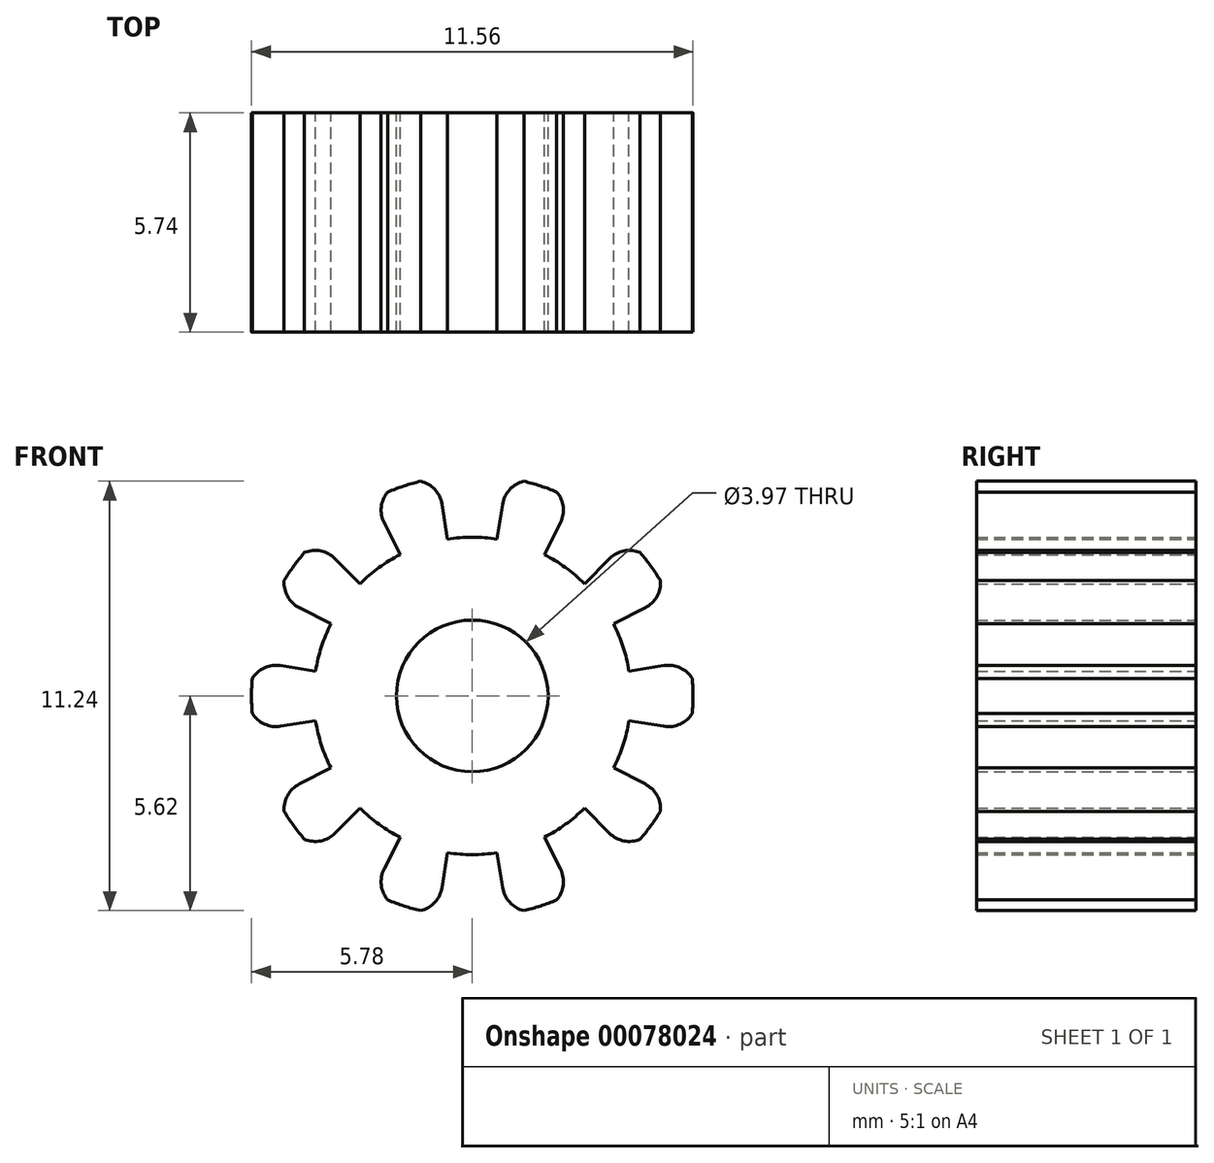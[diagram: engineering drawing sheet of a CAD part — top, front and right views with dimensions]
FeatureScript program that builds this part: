
annotation { "Feature Type Name" : "Feature", "Feature Type Description" : "" }
export const myFeature = defineFeature(function(context is Context, id is Id, definition is map)
    precondition{}
    {
        {
            var Q0;
            Q0=qCreatedBy(makeId("Front.planeOp"),FACE);
            var sketch = newSketch(context, id + "F0", { "sketchPlane" : qUnion([Q0])});
            skCircle(sketch, "E0", {"center": v(0, 0) * mm, "radius": 5.78 * mm, "construction": true});
            skCircle(sketch, "E1", {"center": v(0, 0) * mm, "radius": 5.08 * mm, "construction": true});
            skCircle(sketch, "E2", {"center": v(0, 0) * mm, "radius": 4.15 * mm, "construction": true});
            skLineSegment(sketch, "E3", {"start": v(0, 0) * mm, "end": v(3.95, 1.28) * mm, "construction": true});
            skLineSegment(sketch, "E4", {"start": v(0, 0) * mm, "end": v(6.61, 0) * mm, "construction": true});
            skLineSegment(sketch, "E5", {"start": v(0, 0) * mm, "end": v(6.81, 1.08) * mm, "construction": true});
            skLineSegment(sketch, "E6", {"start": v(0, 0) * mm, "end": v(7.13, 0.56) * mm, "construction": true});
            skArc(sketch, "E7", {"start": v(5.76, 0.45) * mm, "mid": v(5.77, 0.23) * mm, "end": v(5.78, 0) * mm});
            skArc(sketch, "E8", {"start": v(3.95, 1.28) * mm, "mid": v(4.04, 0.97) * mm, "end": v(4.1, 0.65) * mm});
            skLineSegment(sketch, "E9", {"start": v(4.1, 0.65) * mm, "end": v(5.02, 0.8) * mm});
            skArc(sketch, "E10", {"start": v(5.02, 0.8) * mm, "mid": v(5.44, 0.74) * mm, "end": v(5.76, 0.45) * mm});
            skLineSegment(sketch, "E11", {"start": v(0, 0) * mm, "end": v(3.95, 1.28) * mm});
            skLineSegment(sketch, "E12", {"start": v(0, 0) * mm, "end": v(5.78, 0) * mm});
            skArc(sketch, "E13.MirrorCS", {"start": v(3.95, -1.28) * mm, "mid": v(4.04, -0.97) * mm, "end": v(4.1, -0.65) * mm});
            skLineSegment(sketch, "E14.MirrorCS", {"start": v(4.1, -0.65) * mm, "end": v(5.02, -0.8) * mm});
            skArc(sketch, "E15.MirrorCS", {"start": v(5.02, -0.8) * mm, "mid": v(5.44, -0.74) * mm, "end": v(5.76, -0.45) * mm});
            skArc(sketch, "E16.MirrorCS", {"start": v(5.76, -0.45) * mm, "mid": v(5.77, -0.23) * mm, "end": v(5.78, 0) * mm});
            skArc(sketch, "E17.1.0", {"start": v(2.44, 3.36) * mm, "mid": v(2.7, 3.16) * mm, "end": v(2.94, 2.94) * mm});
            skLineSegment(sketch, "E17.1.1", {"start": v(2.94, 2.94) * mm, "end": v(3.6, 3.6) * mm});
            skArc(sketch, "E17.1.2", {"start": v(3.6, 3.6) * mm, "mid": v(3.97, 3.8) * mm, "end": v(4.4, 3.75) * mm});
            skArc(sketch, "E17.1.3", {"start": v(4.4, 3.75) * mm, "mid": v(4.54, 3.58) * mm, "end": v(4.67, 3.4) * mm});
            skArc(sketch, "E17.1.4", {"start": v(4.93, 3.02) * mm, "mid": v(4.8, 3.21) * mm, "end": v(4.67, 3.4) * mm});
            skArc(sketch, "E17.1.5", {"start": v(4.53, 2.3) * mm, "mid": v(4.83, 2.6) * mm, "end": v(4.93, 3.02) * mm});
            skLineSegment(sketch, "E17.1.6", {"start": v(3.7, 1.89) * mm, "end": v(4.53, 2.3) * mm});
            skArc(sketch, "E17.1.7", {"start": v(3.95, 1.28) * mm, "mid": v(3.84, 1.59) * mm, "end": v(3.7, 1.89) * mm});
            skArc(sketch, "E17.2.0", {"start": v(0, 4.15) * mm, "mid": v(0.33, 4.14) * mm, "end": v(0.65, 4.1) * mm});
            skLineSegment(sketch, "E17.2.1", {"start": v(0.65, 4.1) * mm, "end": v(0.8, 5.02) * mm});
            skArc(sketch, "E17.2.2", {"start": v(0.8, 5.02) * mm, "mid": v(0.98, 5.4) * mm, "end": v(1.35, 5.62) * mm});
            skArc(sketch, "E17.2.3", {"start": v(1.35, 5.62) * mm, "mid": v(1.57, 5.56) * mm, "end": v(1.79, 5.5) * mm});
            skArc(sketch, "E17.2.4", {"start": v(2.21, 5.34) * mm, "mid": v(2, 5.42) * mm, "end": v(1.79, 5.5) * mm});
            skArc(sketch, "E17.2.5", {"start": v(2.3, 4.53) * mm, "mid": v(2.38, 4.95) * mm, "end": v(2.21, 5.34) * mm});
            skLineSegment(sketch, "E17.2.6", {"start": v(1.89, 3.7) * mm, "end": v(2.3, 4.53) * mm});
            skArc(sketch, "E17.2.7", {"start": v(2.44, 3.36) * mm, "mid": v(2.17, 3.54) * mm, "end": v(1.89, 3.7) * mm});
            skArc(sketch, "E17.3.0", {"start": v(-2.44, 3.36) * mm, "mid": v(-2.17, 3.54) * mm, "end": v(-1.89, 3.7) * mm});
            skLineSegment(sketch, "E17.3.1", {"start": v(-1.89, 3.7) * mm, "end": v(-2.3, 4.53) * mm});
            skArc(sketch, "E17.3.2", {"start": v(-2.3, 4.53) * mm, "mid": v(-2.38, 4.95) * mm, "end": v(-2.21, 5.34) * mm});
            skArc(sketch, "E17.3.3", {"start": v(-2.21, 5.34) * mm, "mid": v(-2, 5.42) * mm, "end": v(-1.79, 5.5) * mm});
            skArc(sketch, "E17.3.4", {"start": v(-1.35, 5.62) * mm, "mid": v(-1.57, 5.56) * mm, "end": v(-1.79, 5.5) * mm});
            skArc(sketch, "E17.3.5", {"start": v(-0.8, 5.02) * mm, "mid": v(-0.98, 5.4) * mm, "end": v(-1.35, 5.62) * mm});
            skLineSegment(sketch, "E17.3.6", {"start": v(-0.65, 4.1) * mm, "end": v(-0.8, 5.02) * mm});
            skArc(sketch, "E17.3.7", {"start": v(0, 4.15) * mm, "mid": v(-0.33, 4.14) * mm, "end": v(-0.65, 4.1) * mm});
            skArc(sketch, "E17.4.0", {"start": v(-3.95, 1.28) * mm, "mid": v(-3.84, 1.59) * mm, "end": v(-3.7, 1.89) * mm});
            skLineSegment(sketch, "E17.4.1", {"start": v(-3.7, 1.89) * mm, "end": v(-4.53, 2.3) * mm});
            skArc(sketch, "E17.4.2", {"start": v(-4.53, 2.3) * mm, "mid": v(-4.83, 2.6) * mm, "end": v(-4.93, 3.02) * mm});
            skArc(sketch, "E17.4.3", {"start": v(-4.93, 3.02) * mm, "mid": v(-4.8, 3.21) * mm, "end": v(-4.67, 3.4) * mm});
            skArc(sketch, "E17.4.4", {"start": v(-4.4, 3.75) * mm, "mid": v(-4.54, 3.58) * mm, "end": v(-4.67, 3.4) * mm});
            skArc(sketch, "E17.4.5", {"start": v(-3.6, 3.6) * mm, "mid": v(-3.97, 3.8) * mm, "end": v(-4.4, 3.75) * mm});
            skLineSegment(sketch, "E17.4.6", {"start": v(-2.94, 2.94) * mm, "end": v(-3.6, 3.6) * mm});
            skArc(sketch, "E17.4.7", {"start": v(-2.44, 3.36) * mm, "mid": v(-2.7, 3.16) * mm, "end": v(-2.94, 2.94) * mm});
            skArc(sketch, "E17.5.0", {"start": v(-3.95, -1.28) * mm, "mid": v(-4.04, -0.97) * mm, "end": v(-4.1, -0.65) * mm});
            skLineSegment(sketch, "E17.5.1", {"start": v(-4.1, -0.65) * mm, "end": v(-5.02, -0.8) * mm});
            skArc(sketch, "E17.5.2", {"start": v(-5.02, -0.8) * mm, "mid": v(-5.44, -0.74) * mm, "end": v(-5.76, -0.45) * mm});
            skArc(sketch, "E17.5.3", {"start": v(-5.76, -0.45) * mm, "mid": v(-5.77, -0.23) * mm, "end": v(-5.78, 0) * mm});
            skArc(sketch, "E17.5.4", {"start": v(-5.76, 0.45) * mm, "mid": v(-5.77, 0.23) * mm, "end": v(-5.78, 0) * mm});
            skArc(sketch, "E17.5.5", {"start": v(-5.02, 0.8) * mm, "mid": v(-5.44, 0.74) * mm, "end": v(-5.76, 0.45) * mm});
            skLineSegment(sketch, "E17.5.6", {"start": v(-4.1, 0.65) * mm, "end": v(-5.02, 0.8) * mm});
            skArc(sketch, "E17.5.7", {"start": v(-3.95, 1.28) * mm, "mid": v(-4.04, 0.97) * mm, "end": v(-4.1, 0.65) * mm});
            skArc(sketch, "E17.6.0", {"start": v(-2.44, -3.36) * mm, "mid": v(-2.7, -3.16) * mm, "end": v(-2.94, -2.94) * mm});
            skLineSegment(sketch, "E17.6.1", {"start": v(-2.94, -2.94) * mm, "end": v(-3.6, -3.6) * mm});
            skArc(sketch, "E17.6.2", {"start": v(-3.6, -3.6) * mm, "mid": v(-3.97, -3.8) * mm, "end": v(-4.4, -3.75) * mm});
            skArc(sketch, "E17.6.3", {"start": v(-4.4, -3.75) * mm, "mid": v(-4.54, -3.58) * mm, "end": v(-4.67, -3.4) * mm});
            skArc(sketch, "E17.6.4", {"start": v(-4.93, -3.02) * mm, "mid": v(-4.8, -3.21) * mm, "end": v(-4.67, -3.4) * mm});
            skArc(sketch, "E17.6.5", {"start": v(-4.53, -2.3) * mm, "mid": v(-4.83, -2.6) * mm, "end": v(-4.93, -3.02) * mm});
            skLineSegment(sketch, "E17.6.6", {"start": v(-3.7, -1.89) * mm, "end": v(-4.53, -2.3) * mm});
            skArc(sketch, "E17.6.7", {"start": v(-3.95, -1.28) * mm, "mid": v(-3.84, -1.59) * mm, "end": v(-3.7, -1.89) * mm});
            skArc(sketch, "E17.7.0", {"start": v(0, -4.15) * mm, "mid": v(-0.33, -4.14) * mm, "end": v(-0.65, -4.1) * mm});
            skLineSegment(sketch, "E17.7.1", {"start": v(-0.65, -4.1) * mm, "end": v(-0.8, -5.02) * mm});
            skArc(sketch, "E17.7.2", {"start": v(-0.8, -5.02) * mm, "mid": v(-0.98, -5.4) * mm, "end": v(-1.35, -5.62) * mm});
            skArc(sketch, "E17.7.3", {"start": v(-1.35, -5.62) * mm, "mid": v(-1.57, -5.56) * mm, "end": v(-1.79, -5.5) * mm});
            skArc(sketch, "E17.7.4", {"start": v(-2.21, -5.34) * mm, "mid": v(-2, -5.42) * mm, "end": v(-1.79, -5.5) * mm});
            skArc(sketch, "E17.7.5", {"start": v(-2.3, -4.53) * mm, "mid": v(-2.38, -4.95) * mm, "end": v(-2.21, -5.34) * mm});
            skLineSegment(sketch, "E17.7.6", {"start": v(-1.89, -3.7) * mm, "end": v(-2.3, -4.53) * mm});
            skArc(sketch, "E17.7.7", {"start": v(-2.44, -3.36) * mm, "mid": v(-2.17, -3.54) * mm, "end": v(-1.89, -3.7) * mm});
            skArc(sketch, "E17.8.0", {"start": v(2.44, -3.36) * mm, "mid": v(2.17, -3.54) * mm, "end": v(1.89, -3.7) * mm});
            skLineSegment(sketch, "E17.8.1", {"start": v(1.89, -3.7) * mm, "end": v(2.3, -4.53) * mm});
            skArc(sketch, "E17.8.2", {"start": v(2.3, -4.53) * mm, "mid": v(2.38, -4.95) * mm, "end": v(2.21, -5.34) * mm});
            skArc(sketch, "E17.8.3", {"start": v(2.21, -5.34) * mm, "mid": v(2, -5.42) * mm, "end": v(1.79, -5.5) * mm});
            skArc(sketch, "E17.8.4", {"start": v(1.35, -5.62) * mm, "mid": v(1.57, -5.56) * mm, "end": v(1.79, -5.5) * mm});
            skArc(sketch, "E17.8.5", {"start": v(0.8, -5.02) * mm, "mid": v(0.98, -5.4) * mm, "end": v(1.35, -5.62) * mm});
            skLineSegment(sketch, "E17.8.6", {"start": v(0.65, -4.1) * mm, "end": v(0.8, -5.02) * mm});
            skArc(sketch, "E17.8.7", {"start": v(0, -4.15) * mm, "mid": v(0.33, -4.14) * mm, "end": v(0.65, -4.1) * mm});
            skArc(sketch, "E17.9.0", {"start": v(3.95, -1.28) * mm, "mid": v(3.84, -1.59) * mm, "end": v(3.7, -1.89) * mm});
            skLineSegment(sketch, "E17.9.1", {"start": v(3.7, -1.89) * mm, "end": v(4.53, -2.3) * mm});
            skArc(sketch, "E17.9.2", {"start": v(4.53, -2.3) * mm, "mid": v(4.83, -2.6) * mm, "end": v(4.93, -3.02) * mm});
            skArc(sketch, "E17.9.3", {"start": v(4.93, -3.02) * mm, "mid": v(4.8, -3.21) * mm, "end": v(4.67, -3.4) * mm});
            skArc(sketch, "E17.9.4", {"start": v(4.4, -3.75) * mm, "mid": v(4.54, -3.58) * mm, "end": v(4.67, -3.4) * mm});
            skArc(sketch, "E17.9.5", {"start": v(3.6, -3.6) * mm, "mid": v(3.97, -3.8) * mm, "end": v(4.4, -3.75) * mm});
            skLineSegment(sketch, "E17.9.6", {"start": v(2.94, -2.94) * mm, "end": v(3.6, -3.6) * mm});
            skArc(sketch, "E17.9.7", {"start": v(2.44, -3.36) * mm, "mid": v(2.7, -3.16) * mm, "end": v(2.94, -2.94) * mm});
            skCircle(sketch, "E18", {"center": v(0, 0) * mm, "radius": 1.98 * mm});
            skSolve(sketch);
        }
        {
            var Q0;
            Q0 = qSketchRegion(id + "F0", true);
            extrude(context, id + "F1", {"entities" : qUnion([Q0]), "endBound" : BoundingType.SYMMETRIC, "depth" : 5.74 * mm});
        }
    });
